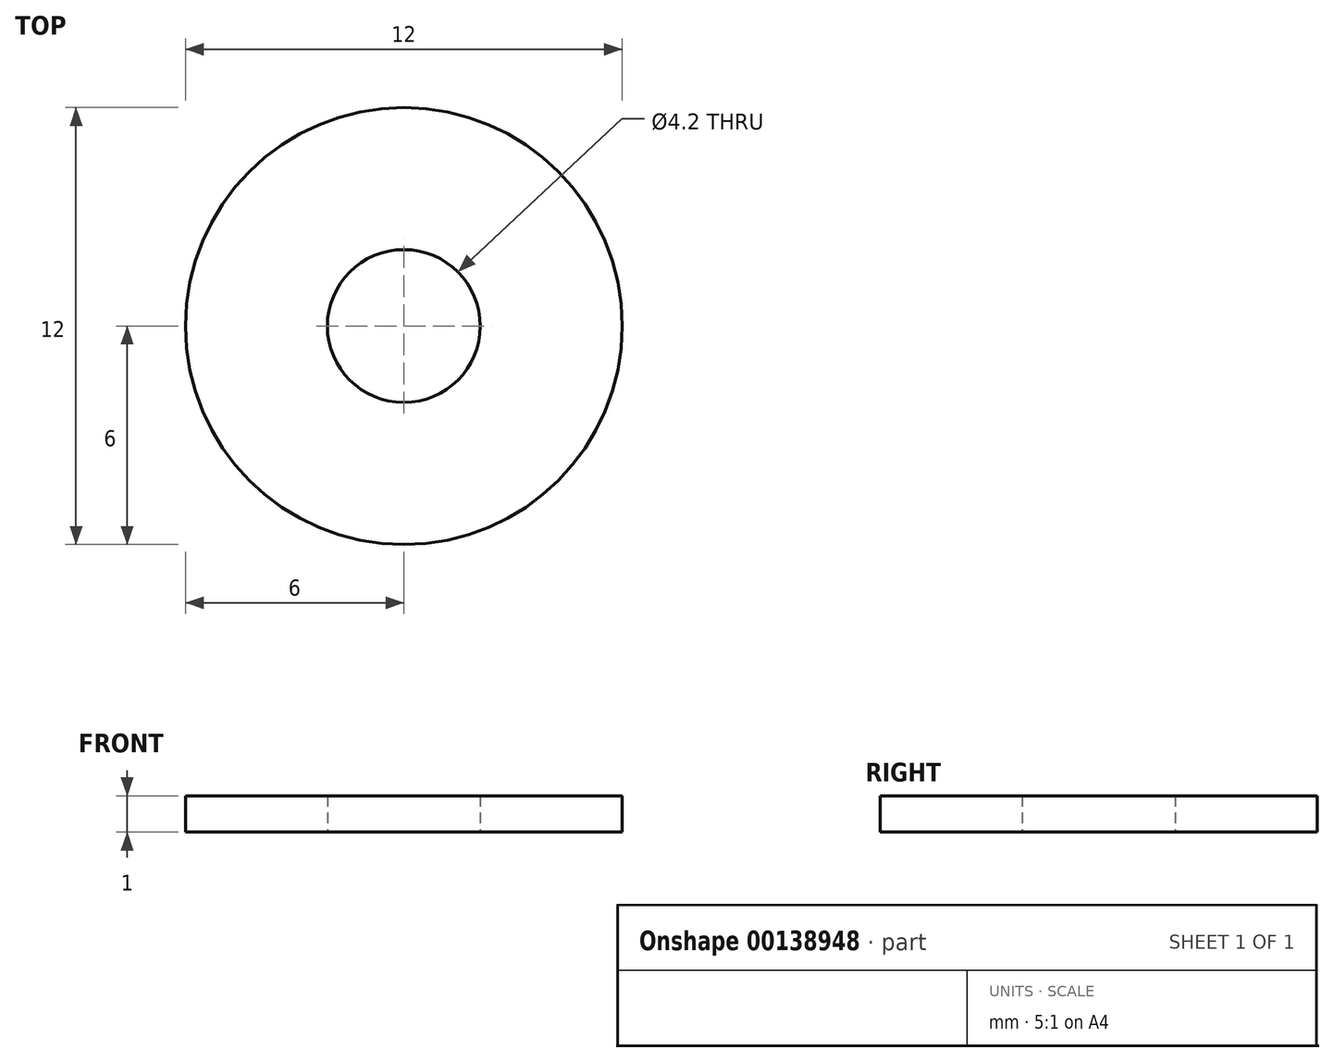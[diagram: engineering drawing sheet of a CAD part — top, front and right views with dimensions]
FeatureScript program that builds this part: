
annotation { "Feature Type Name" : "Feature", "Feature Type Description" : "" }
export const myFeature = defineFeature(function(context is Context, id is Id, definition is map)
    precondition{}
    {
        {
            var Q0;
            Q0=qCreatedBy(makeId("Top.planeOp"),FACE);
            var sketch = newSketch(context, id + "F0", { "sketchPlane" : qUnion([Q0])});
            skCircle(sketch, "E0", {"center": v(0, 0) * mm, "radius": 6 * mm});
            skCircle(sketch, "E1", {"center": v(0, 0) * mm, "radius": 2.1 * mm});
            skSolve(sketch);
        }
        {
            var Q0;
            Q0=makeQuery(id+"F0.imprint","IMPRINT",FACE,{"disambiguationData":[TD([[makeQuery(id+"F0.imprint","IMPRINT",EDGE,{"derivedFrom":sQuery(id+"F0.wireOp",EDGE,"E0")}),1.0]])]});
            extrude(context, id + "F1", {"entities" : qUnion([Q0]), "depth" : 1 * mm});
        }
    });
